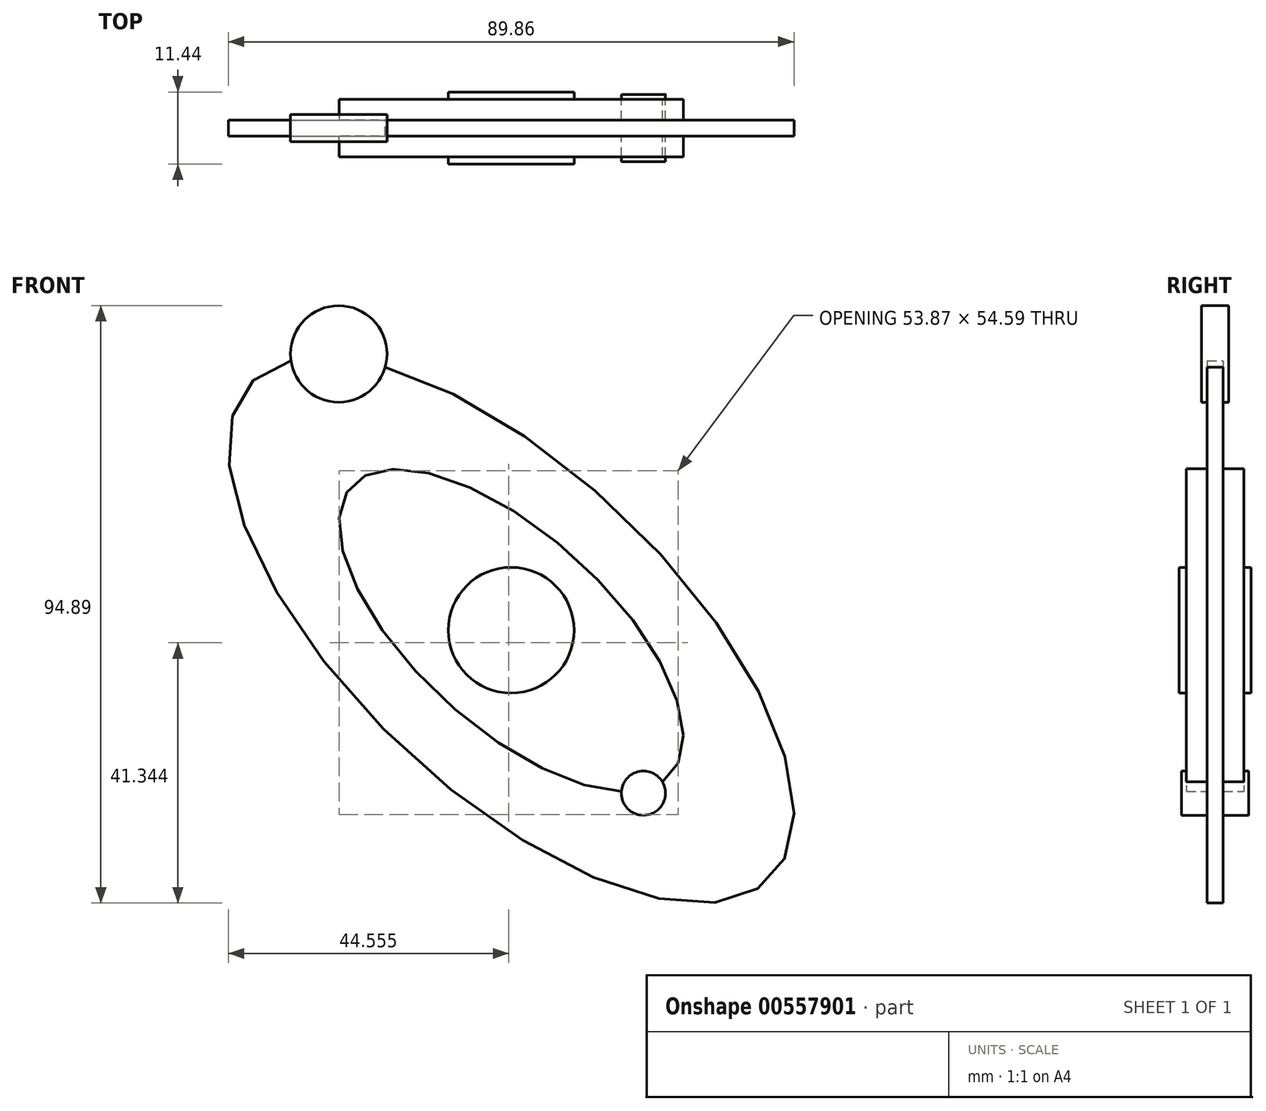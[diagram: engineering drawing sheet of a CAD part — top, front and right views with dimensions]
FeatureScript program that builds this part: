
annotation { "Feature Type Name" : "Feature", "Feature Type Description" : "" }
export const myFeature = defineFeature(function(context is Context, id is Id, definition is map)
    precondition{}
    {
        {
            var Q0;
            Q0=qCreatedBy(makeId("Front.planeOp"),FACE);
            var sketch = newSketch(context, id + "F0", { "sketchPlane" : qUnion([Q0])});
            skEllipse(sketch, "E0", {"center": v(0, 0) * mm, "majorRadius": 57.03 * mm, "minorRadius": 25.38 * mm, "majorAxis": v(-0.73, 0.69)});
            skCircle(sketch, "E1", {"center": v(-27.38, 43.88) * mm, "radius": 7.67 * mm});
            skPoint(sketch, "E1.first.point", {"position": v(-34.97, 42.8) * mm});
            skPoint(sketch, "E1.second.point", {"position": v(-19.77, 44.8) * mm});
            skPoint(sketch, "E1.third.point", {"position": v(-20.02, 41.76) * mm});
            skEllipse(sketch, "E2", {"center": v(0, 0) * mm, "majorRadius": 34.2 * mm, "minorRadius": 15.34 * mm, "majorAxis": v(-0.74, 0.67)});
            skCircle(sketch, "E3", {"center": v(21, -25.87) * mm, "radius": 3.5 * mm});
            skPoint(sketch, "E3.first.point", {"position": v(17.5, -25.6) * mm});
            skPoint(sketch, "E3.second.point", {"position": v(24.3, -27.08) * mm});
            skPoint(sketch, "E3.third.point", {"position": v(24.5, -25.64) * mm});
            skCircle(sketch, "E4", {"center": v(0, 0) * mm, "radius": 10 * mm});
            skSolve(sketch);
        }
        {
            var Q0;
            {var subQ0=sQuery(id+"F0.wireOp",EDGE,"E3");var subQ1=sQuery(id+"F0.wireOp",EDGE,"E2");var subQ2=makeQuery(id+"F0.imprint","INTERSECT",VERTEX,{"disambiguationData":[OD(0.0)],"derivedFrom":[subQ1,subQ0]});Q0=makeQuery(id+"F0.imprint","IMPRINT",FACE,{"disambiguationData":[TD([[makeQuery(id+"F0.imprint","IMPRINT",EDGE,{"disambiguationData":[TD([[subQ2,1.0]])],"derivedFrom":subQ1}),1.0]])]});}
            extrude(context, id + "F1", {"entities" : qUnion([Q0]), "endBound" : BoundingType.SYMMETRIC, "depth" : 9.14 * mm, "offsetDistance" : 25.4 * mm});
        }
        {
            var Q0;
            {var subQ0=sQuery(id+"F0.wireOp",EDGE,"E1");var subQ1=sQuery(id+"F0.wireOp",EDGE,"E0");var subQ2=makeQuery(id+"F0.imprint","INTERSECT",VERTEX,{"disambiguationData":[OD(0.0)],"derivedFrom":[subQ1,subQ0]});Q0=makeQuery(id+"F0.imprint","IMPRINT",FACE,{"disambiguationData":[TD([[makeQuery(id+"F0.imprint","IMPRINT",EDGE,{"disambiguationData":[TD([[subQ2,-1.0]])],"derivedFrom":subQ1}),1.0]])]});}
            extrude(context, id + "F2", {"entities" : qUnion([Q0]), "operationType" : NewBodyOperationType.ADD, "endBound" : BoundingType.SYMMETRIC, "depth" : 2.54 * mm, "offsetDistance" : 25.4 * mm});
        }
        {
            var Q0;
            {var subQ0=sQuery(id+"F0.wireOp",EDGE,"E1");var subQ1=sQuery(id+"F0.wireOp",EDGE,"E0");var subQ2=makeQuery(id+"F0.imprint","INTERSECT",VERTEX,{"disambiguationData":[OD(0.0)],"derivedFrom":[subQ1,subQ0]});Q0=makeQuery(id+"F0.imprint","IMPRINT",FACE,{"disambiguationData":[TD([[makeQuery(id+"F0.imprint","IMPRINT",EDGE,{"disambiguationData":[TD([[subQ2,1.0]])],"derivedFrom":subQ1}),1.0]])]});}
            var Q1;
            {var subQ0=sQuery(id+"F0.wireOp",EDGE,"E1");var subQ1=sQuery(id+"F0.wireOp",EDGE,"E0");var subQ2=makeQuery(id+"F0.imprint","INTERSECT",VERTEX,{"disambiguationData":[OD(0.0)],"derivedFrom":[subQ1,subQ0]});Q1=makeQuery(id+"F0.imprint","IMPRINT",FACE,{"disambiguationData":[TD([[makeQuery(id+"F0.imprint","IMPRINT",EDGE,{"disambiguationData":[TD([[subQ2,1.0]])],"derivedFrom":subQ1}),-1.0]])]});}
            extrude(context, id + "F3", {"entities" : qUnion([Q0, Q1]), "operationType" : NewBodyOperationType.ADD, "endBound" : BoundingType.SYMMETRIC, "depth" : 4.32 * mm, "offsetDistance" : 25.4 * mm});
        }
        {
            var Q0;
            {var subQ0=sQuery(id+"F0.wireOp",EDGE,"E3");var subQ1=sQuery(id+"F0.wireOp",EDGE,"E2");var subQ2=makeQuery(id+"F0.imprint","INTERSECT",VERTEX,{"disambiguationData":[OD(0.0)],"derivedFrom":[subQ1,subQ0]});Q0=makeQuery(id+"F0.imprint","IMPRINT",FACE,{"disambiguationData":[TD([[makeQuery(id+"F0.imprint","IMPRINT",EDGE,{"disambiguationData":[TD([[subQ2,-1.0]])],"derivedFrom":subQ1}),-1.0]])]});}
            var Q1;
            {var subQ0=sQuery(id+"F0.wireOp",EDGE,"E3");var subQ1=sQuery(id+"F0.wireOp",EDGE,"E2");var subQ2=makeQuery(id+"F0.imprint","INTERSECT",VERTEX,{"disambiguationData":[OD(0.0)],"derivedFrom":[subQ1,subQ0]});Q1=makeQuery(id+"F0.imprint","IMPRINT",FACE,{"disambiguationData":[TD([[makeQuery(id+"F0.imprint","IMPRINT",EDGE,{"disambiguationData":[TD([[subQ2,-1.0]])],"derivedFrom":subQ1}),1.0]])]});}
            extrude(context, id + "F4", {"entities" : qUnion([Q0, Q1]), "operationType" : NewBodyOperationType.ADD, "endBound" : BoundingType.SYMMETRIC, "depth" : 10.67 * mm, "offsetDistance" : 25.4 * mm});
        }
        {
            var Q0;
            Q0=makeQuery(id+"F0.imprint","IMPRINT",FACE,{"disambiguationData":[TD([[makeQuery(id+"F0.imprint","IMPRINT",EDGE,{"derivedFrom":sQuery(id+"F0.wireOp",EDGE,"E4")}),1.0]])]});
            extrude(context, id + "F5", {"entities" : qUnion([Q0]), "operationType" : NewBodyOperationType.ADD, "endBound" : BoundingType.SYMMETRIC, "depth" : 11.43 * mm, "offsetDistance" : 25.4 * mm});
        }
    });
